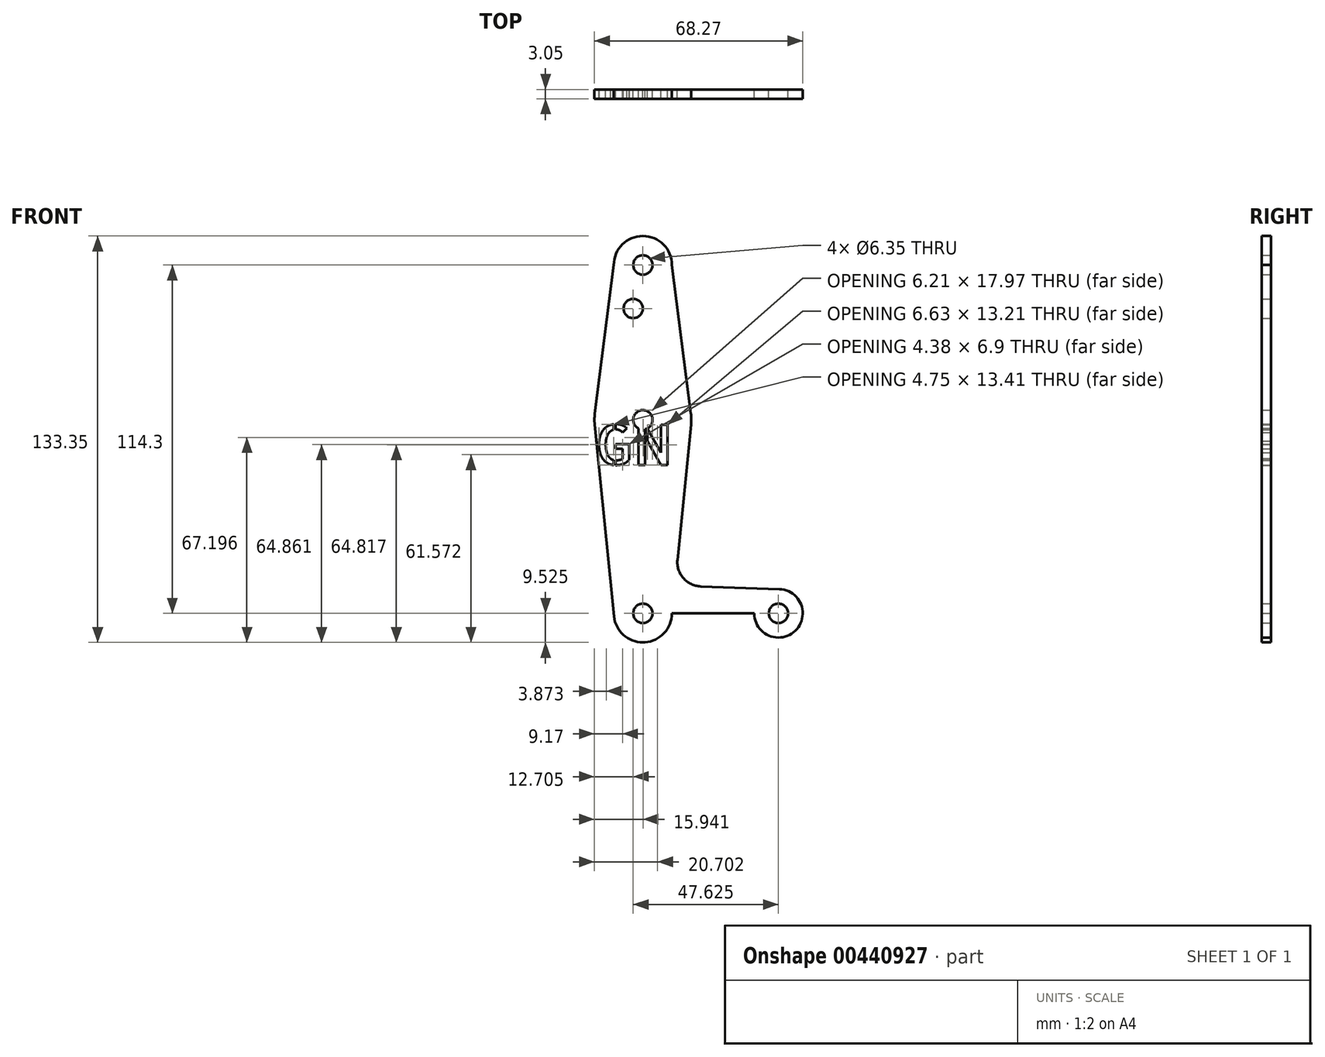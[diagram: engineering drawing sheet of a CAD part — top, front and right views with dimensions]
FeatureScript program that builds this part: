
annotation { "Feature Type Name" : "Feature", "Feature Type Description" : "" }
export const myFeature = defineFeature(function(context is Context, id is Id, definition is map)
    precondition{}
    {
        {
            var Q0;
            Q0=qCreatedBy(makeId("Front.planeOp"),FACE);
            var sketch = newSketch(context, id + "F0", { "sketchPlane" : qUnion([Q0])});
            skCircle(sketch, "E0", {"center": v(0, 66.68) * mm, "radius": 9.53 * mm});
            skCircle(sketch, "E1", {"center": v(0, 15.88) * mm, "radius": 15.88 * mm});
            skCircle(sketch, "E2", {"center": v(0, -47.62) * mm, "radius": 9.53 * mm});
            skCircle(sketch, "E3", {"center": v(44.45, -47.62) * mm, "radius": 7.94 * mm});
            skLineSegment(sketch, "E4", {"start": v(0, 66.68) * mm, "end": v(0, 15.88) * mm});
            skLineSegment(sketch, "E5", {"start": v(0, -47.62) * mm, "end": v(0, 15.88) * mm});
            skLineSegment(sketch, "E6", {"start": v(0, -47.62) * mm, "end": v(44.45, -47.62) * mm});
            skLineSegment(sketch, "E7", {"start": v(-9.53, 66.68) * mm, "end": v(-15.75, 17.88) * mm});
            skLineSegment(sketch, "E8", {"start": v(9.52, 66.68) * mm, "end": v(15.75, 17.88) * mm});
            skLineSegment(sketch, "E9", {"start": v(0, 66.68) * mm, "end": v(-9.53, 66.68) * mm, "construction": true});
            skLineSegment(sketch, "E10", {"start": v(0, 66.68) * mm, "end": v(9.52, 66.68) * mm, "construction": true});
            skLineSegment(sketch, "E11", {"start": v(-15.8, 14.29) * mm, "end": v(-9.48, -48.58) * mm});
            skLineSegment(sketch, "E12", {"start": v(15.8, 14.29) * mm, "end": v(11.34, -30.04) * mm});
            skLineSegment(sketch, "E13", {"start": v(18.97, -38.78) * mm, "end": v(44.73, -39.7) * mm});
            skLineSegment(sketch, "E14", {"start": v(0, -57.15) * mm, "end": v(44.73, -55.56) * mm});
            skCircle(sketch, "E15", {"center": v(0, 66.68) * mm, "radius": 3.18 * mm});
            skCircle(sketch, "E16", {"center": v(-3.17, 52.4) * mm, "radius": 3.18 * mm});
            skCircle(sketch, "E17", {"center": v(0, -47.62) * mm, "radius": 3.18 * mm});
            skCircle(sketch, "E18", {"center": v(44.45, -47.62) * mm, "radius": 3.18 * mm});
            skCircle(sketch, "E19", {"center": v(0, 15.88) * mm, "radius": 3.18 * mm});
            skArc(sketch, "E20.filletArc", {"start": v(11.34, -30.04) * mm, "mid": v(13.26, -36.06) * mm, "end": v(18.97, -38.78) * mm});
            skText(sketch, "E21", { "text": "GN", "fontName": "AllertaStencil-Regular.ttf"});
            const initialGuessF0  = {"E21": [-0.0158, 0.00106, 1, 0, 0.01322]};
            skSetInitialGuess(sketch, initialGuessF0);
            skSolve(sketch);
        }
        {
            var Q0;
            {var subQ1=sQuery(id+"F0.wireOp",EDGE,"E1");var subQ5=makeQuery(id+"F0.imprint","INTERSECT",VERTEX,{"derivedFrom":[subQ1,sQuery(id+"F0.wireOp",EDGE,"E8")]});Q0=makeQuery(id+"F0.imprint","IMPRINT",FACE,{"disambiguationData":[TD([[makeQuery(id+"F0.imprint","IMPRINT",EDGE,{"disambiguationData":[TD([[subQ5,-1.0]])],"derivedFrom":subQ1}),1.0]])]});}
            var Q1;
            Q1=makeQuery(id+"F0.imprint","IMPRINT",FACE,{"disambiguationData":[TD([[makeQuery(id+"F0.imprint","IMPRINT",EDGE,{"derivedFrom":sQuery(id+"F0.wireOp",EDGE,"E18")}),-1.0]])]});
            var Q2;
            {var subQ5=sQuery(id+"F0.wireOp",EDGE,"E7");Q2=makeQuery(id+"F0.imprint","IMPRINT",FACE,{"disambiguationData":[TD([[makeQuery(id+"F0.imprint","IMPRINT",EDGE,{"derivedFrom":subQ5}),1.0]])]});}
            var Q3;
            {var subQ0=sQuery(id+"F0.wireOp",EDGE,"E1");var subQ4=makeQuery(id+"F0.imprint","INTERSECT",VERTEX,{"derivedFrom":[subQ0,sQuery(id+"F0.wireOp",EDGE,"E7")]});Q3=makeQuery(id+"F0.imprint","IMPRINT",FACE,{"disambiguationData":[TD([[makeQuery(id+"F0.imprint","IMPRINT",EDGE,{"disambiguationData":[TD([[subQ4,1.0]])],"derivedFrom":subQ0}),1.0]])]});}
            var Q4;
            Q4=makeQuery(id+"F0.imprint","IMPRINT",FACE,{"disambiguationData":[TD([[makeQuery(id+"F0.imprint","IMPRINT",EDGE,{"derivedFrom":sQuery(id+"F0.wireOp",EDGE,"E15")}),-1.0]])]});
            var Q5;
            {var subQ4=sQuery(id+"F0.wireOp",EDGE,"E8");Q5=makeQuery(id+"F0.imprint","IMPRINT",FACE,{"disambiguationData":[TD([[makeQuery(id+"F0.imprint","IMPRINT",EDGE,{"derivedFrom":subQ4}),-1.0]])]});}
            var Q6;
            {var subQ0=sQuery(id+"F0.wireOp",EDGE,"E11");Q6=makeQuery(id+"F0.imprint","IMPRINT",FACE,{"disambiguationData":[TD([[makeQuery(id+"F0.imprint","IMPRINT",EDGE,{"derivedFrom":subQ0}),1.0]])]});}
            var Q7;
            {var subQ0=sQuery(id+"F0.wireOp",EDGE,"E5");var subQ1=sQuery(id+"F0.wireOp",EDGE,"E2");var subQ2=makeQuery(id+"F0.imprint","INTERSECT",VERTEX,{"derivedFrom":[subQ1,subQ0]});Q7=makeQuery(id+"F0.imprint","IMPRINT",FACE,{"disambiguationData":[TD([[makeQuery(id+"F0.imprint","IMPRINT",EDGE,{"disambiguationData":[TD([[subQ2,1.0]])],"derivedFrom":subQ1}),1.0]])]});}
            var Q8;
            {var subQ0=sQuery(id+"F0.wireOp",EDGE,"E14");var subQ1=sQuery(id+"F0.wireOp",EDGE,"E2");var subQ2=makeQuery(id+"F0.imprint","INTERSECT",VERTEX,{"disambiguationData":[OD(1.0)],"derivedFrom":[subQ1,subQ0]});Q8=makeQuery(id+"F0.imprint","IMPRINT",FACE,{"disambiguationData":[TD([[makeQuery(id+"F0.imprint","IMPRINT",EDGE,{"disambiguationData":[TD([[subQ2,-1.0]])],"derivedFrom":subQ1}),-1.0]])]});}
            var Q9;
            {var subQ10=sQuery(id+"F0.wireOp",EDGE,"E12");Q9=makeQuery(id+"F0.imprint","IMPRINT",FACE,{"disambiguationData":[TD([[makeQuery(id+"F0.imprint","IMPRINT",EDGE,{"derivedFrom":subQ10}),-1.0]])]});}
            var Q10;
            {var subQ1=sQuery(id+"F0.wireOp",EDGE,"E2");var subQ5=makeQuery(id+"F0.imprint","INTERSECT",VERTEX,{"derivedFrom":[subQ1,sQuery(id+"F0.wireOp",EDGE,"E11")]});Q10=makeQuery(id+"F0.imprint","IMPRINT",FACE,{"disambiguationData":[TD([[makeQuery(id+"F0.imprint","IMPRINT",EDGE,{"disambiguationData":[TD([[subQ5,1.0]])],"derivedFrom":subQ1}),1.0]])]});}
            var Q11;
            {var subQ0=sQuery(id+"F0.wireOp",EDGE,"E14");var subQ1=sQuery(id+"F0.wireOp",EDGE,"E2");var subQ2=makeQuery(id+"F0.imprint","INTERSECT",VERTEX,{"disambiguationData":[OD(0.0)],"derivedFrom":[subQ1,subQ0]});Q11=makeQuery(id+"F0.imprint","IMPRINT",FACE,{"disambiguationData":[TD([[makeQuery(id+"F0.imprint","IMPRINT",EDGE,{"disambiguationData":[TD([[subQ2,-1.0]])],"derivedFrom":subQ1}),1.0]])]});}
            extrude(context, id + "F1", {"entities" : qUnion([Q0, Q1, Q2, Q3, Q4, Q5, Q6, Q7, Q8, Q9, Q10, Q11]), "depth" : 3.05 * mm});
        }
    });
